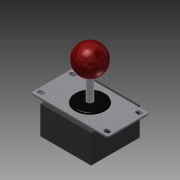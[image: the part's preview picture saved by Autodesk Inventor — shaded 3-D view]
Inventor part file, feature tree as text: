
AUTODESK INVENTOR PART (.ipt)
format: ipt  version: 2013 (Build 170138000, 138)  size: 222,720 bytes
history: native  units: mm
features: sketch x6, extrude x5, fillet x5, revolve x1
ambient origin geometry x8: Origin, YZ Plane, XZ Plane, XY Plane, X Axis, Y Axis, Z Axis, Center Point
bodies: Solid1 (feature_tree)
feature tree (17):
  extrude  "Extrusion1"  Depth=53.0mm
  extrude  "Extrusion4"  Depth=5.5mm
  extrude  "Extrusion5"  Depth=20.25mm
  extrude  "Extrusion6"  Depth=20.0mm
  extrude  "Extrusion7"  Depth=38.0mm
  revolve  "Revolution1"  [1 undecoded]
  fillet  "Fillet1"  Radius=46.0mm
  fillet  "Fillet2"  Radius=65.0mm
  fillet  "Fillet3"  Radius=62.0mm
  fillet  "Fillet4"  Radius=36.0mm
  fillet  "Fillet5"  [1 undecoded]
  sketch  "Sketch2"  dims[d5=98.0mm d7=53.0mm]
  sketch  "Sketch3"  dims[d8=2.0mm d9=0.0mm d10=5.5mm]
  sketch  "Sketch4"  dims[d13=2.5mm d14=20.25mm]
  sketch  "Sketch5"  dims[d15=41.25mm d18=20.0mm d20=85.0mm d21=20.0mm d23=40.5mm]
  sketch  "Sketch6"  dims[d28=2.0mm d29=0.0mm d30=38.0mm]
  sketch  "Sketch7"  dims[d32=2.0mm d33=0.0mm d34=8.0mm d37=46.0mm d38=0.0mm d39=65.0mm d42=62.0mm d43=36.0mm d44=0.0mm d45=90.0deg d46=36.0mm d50=2.0mm d51=2.0mm d52=2.0mm d53=2.0mm d55=2.0mm]
note: 2 required parameter values undecoded (feature->parameter linkage not recoverable at this tier; creation-order binding heuristic only, values carry confidence <= 0.55)